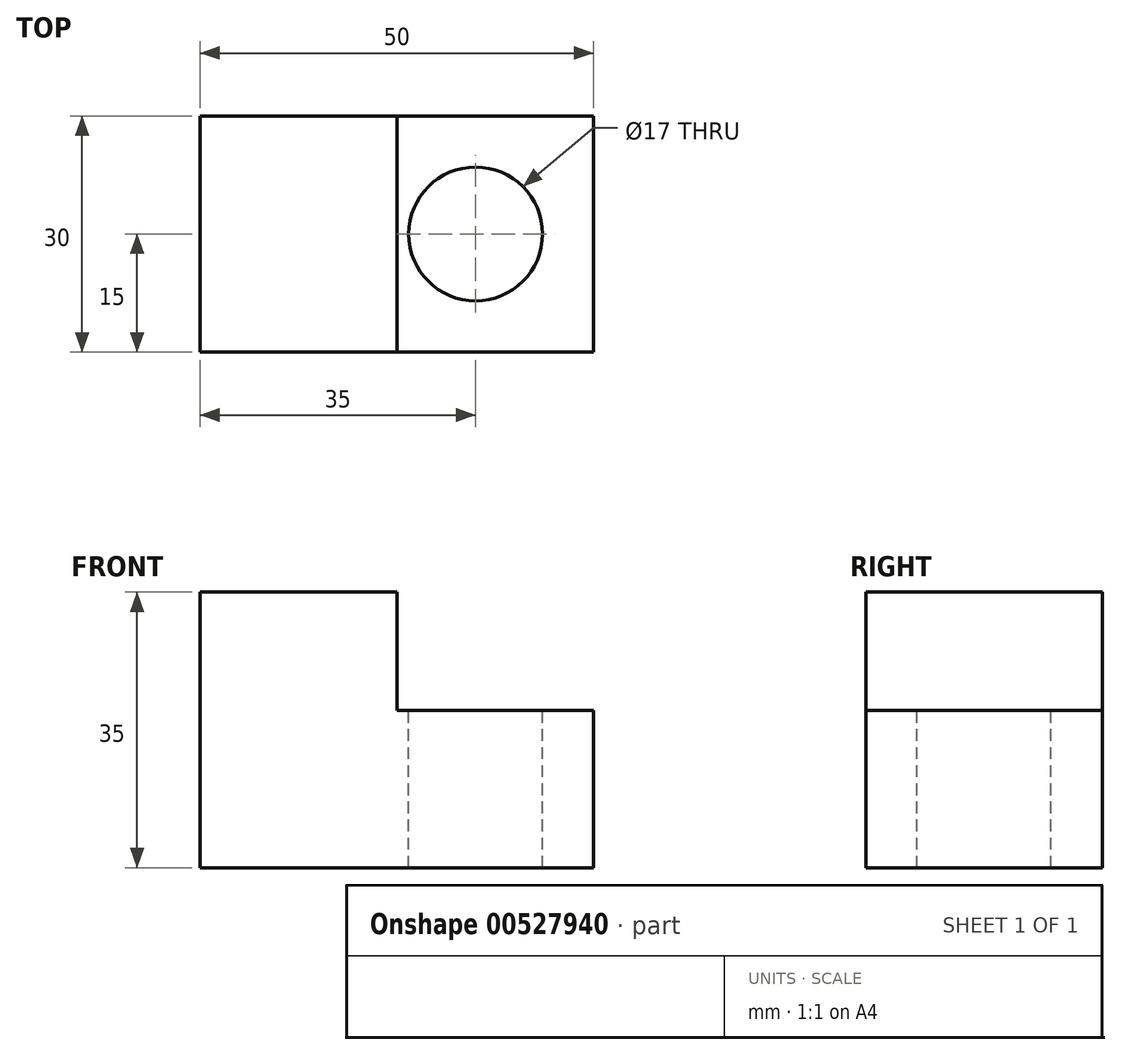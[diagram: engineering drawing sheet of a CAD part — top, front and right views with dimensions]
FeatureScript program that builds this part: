
annotation { "Feature Type Name" : "Feature", "Feature Type Description" : "" }
export const myFeature = defineFeature(function(context is Context, id is Id, definition is map)
    precondition{}
    {
        {
            var Q0;
            Q0=qCreatedBy(makeId("Front.planeOp"),FACE);
            var sketch = newSketch(context, id + "F0", { "sketchPlane" : qUnion([Q0])});
            skLineSegment(sketch, "E0.bottom", {"start": v(0, 0) * mm, "end": v(50, 0) * mm});
            skLineSegment(sketch, "E0.top", {"start": v(0, 35) * mm, "end": v(50, 35) * mm});
            skLineSegment(sketch, "E0.left", {"start": v(0, 0) * mm, "end": v(0, 35) * mm});
            skLineSegment(sketch, "E0.right", {"start": v(50, 0) * mm, "end": v(50, 35) * mm});
            skSolve(sketch);
        }
        {
            var Q0;
            Q0 = qSketchRegion(id + "F0", true);
            extrude(context, id + "F1", {"entities" : qUnion([Q0]), "depth" : 30 * mm, "offsetDistance" : 25.4 * mm});
        }
        {
            var Q0;
            Q0=makeQuery(id+"F1.opExtrude","CAP_FACE",FACE,{"disambiguationData":[OSD([sQuery(id+"F0.wireOp",EDGE,"E0.bottom"),sQuery(id+"F0.wireOp",EDGE,"E0.top"),sQuery(id+"F0.wireOp",EDGE,"E0.left"),sQuery(id+"F0.wireOp",EDGE,"E0.right")])],"isStart":false});
            var sketch = newSketch(context, id + "F2", { "sketchPlane" : qUnion([Q0])});
            skLineSegment(sketch, "E1.bottom", {"start": v(50, 35) * mm, "end": v(25, 35) * mm});
            skLineSegment(sketch, "E1.top", {"start": v(50, 20) * mm, "end": v(25, 20) * mm});
            skLineSegment(sketch, "E1.left", {"start": v(50, 35) * mm, "end": v(50, 20) * mm});
            skLineSegment(sketch, "E1.right", {"start": v(25, 35) * mm, "end": v(25, 20) * mm});
            skSolve(sketch);
        }
        {
            var Q0;
            Q0 = qSketchRegion(id + "F2", true);
            extrude(context, id + "F3", {"entities" : qUnion([Q0]), "operationType" : NewBodyOperationType.REMOVE, "endBound" : BoundingType.THROUGH_ALL, "oppositeDirection" : true, "depth" : 25.4 * mm, "offsetDistance" : 25.4 * mm});
        }
        {
            var Q0;
            Q0=makeQuery(id+"F3.boolean.opBoolean","COPY",FACE,{"derivedFrom":makeQuery(id+"F3.opExtrude","SWEPT_FACE",FACE,{"disambiguationData":[OSD([sQuery(id+"F2.wireOp",EDGE,"E1.top")])]})});
            var sketch = newSketch(context, id + "F4", { "sketchPlane" : qUnion([Q0])});
            skCircle(sketch, "E2", {"center": v(35, -15) * mm, "radius": 8.5 * mm});
            skSolve(sketch);
        }
        {
            var Q0;
            Q0 = qSketchRegion(id + "F4", true);
            extrude(context, id + "F5", {"entities" : qUnion([Q0]), "operationType" : NewBodyOperationType.REMOVE, "endBound" : BoundingType.THROUGH_ALL, "oppositeDirection" : true, "depth" : 25.4 * mm, "offsetDistance" : 25.4 * mm});
        }
    });
